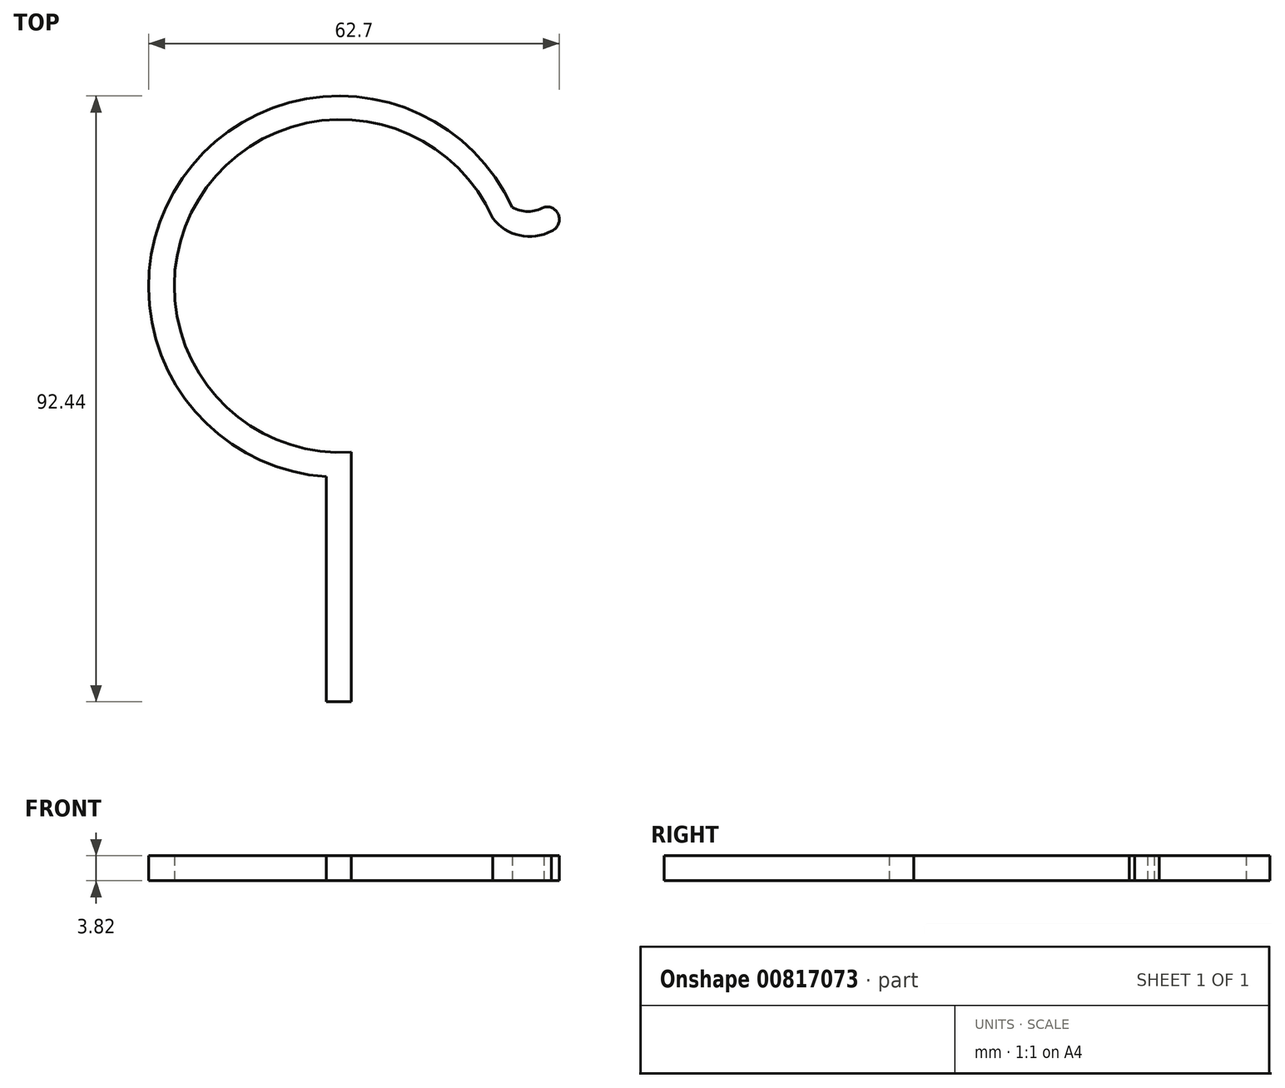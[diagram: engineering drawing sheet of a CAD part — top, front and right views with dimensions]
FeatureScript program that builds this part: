
annotation { "Feature Type Name" : "Feature", "Feature Type Description" : "" }
export const myFeature = defineFeature(function(context is Context, id is Id, definition is map)
    precondition{}
    {
        {
            var Q0;
            Q0=qCreatedBy(makeId("Top.planeOp"),FACE);
            var sketch = newSketch(context, id + "F0", { "sketchPlane" : qUnion([Q0])});
            skLineSegment(sketch, "E0", {"start": v(0, 0) * mm, "end": v(0, -38.1) * mm});
            skLineSegment(sketch, "E1", {"start": v(0, -38.1) * mm, "end": v(-3.81, -38.1) * mm});
            skArc(sketch, "E2", {"start": v(21.6, 35.69) * mm, "mid": v(-23.32, 38.5) * mm, "end": v(0, 0) * mm});
            skLineSegment(sketch, "E3", {"start": v(-3.81, -38.1) * mm, "end": v(-3.81, -3.76) * mm});
            skArc(sketch, "E4", {"start": v(24.6, 37.38) * mm, "mid": v(-25.78, 41.78) * mm, "end": v(-3.81, -3.76) * mm});
            skArc(sketch, "E5", {"start": v(21.6, 35.69) * mm, "mid": v(25.73, 33.06) * mm, "end": v(30.56, 33.74) * mm});
            skArc(sketch, "E6", {"start": v(24.6, 37.38) * mm, "mid": v(27, 36.72) * mm, "end": v(29.4, 37.38) * mm});
            skArc(sketch, "E7", {"start": v(30.56, 33.74) * mm, "mid": v(31.68, 36.1) * mm, "end": v(29.4, 37.38) * mm});
            skSolve(sketch);
        }
        {
            var Q0;
            Q0 = qSketchRegion(id + "F0", true);
            extrude(context, id + "F1", {"entities" : qUnion([Q0]), "endBound" : BoundingType.SYMMETRIC, "depth" : 3.8 * mm, "offsetDistance" : 25.4 * mm});
        }
    });
